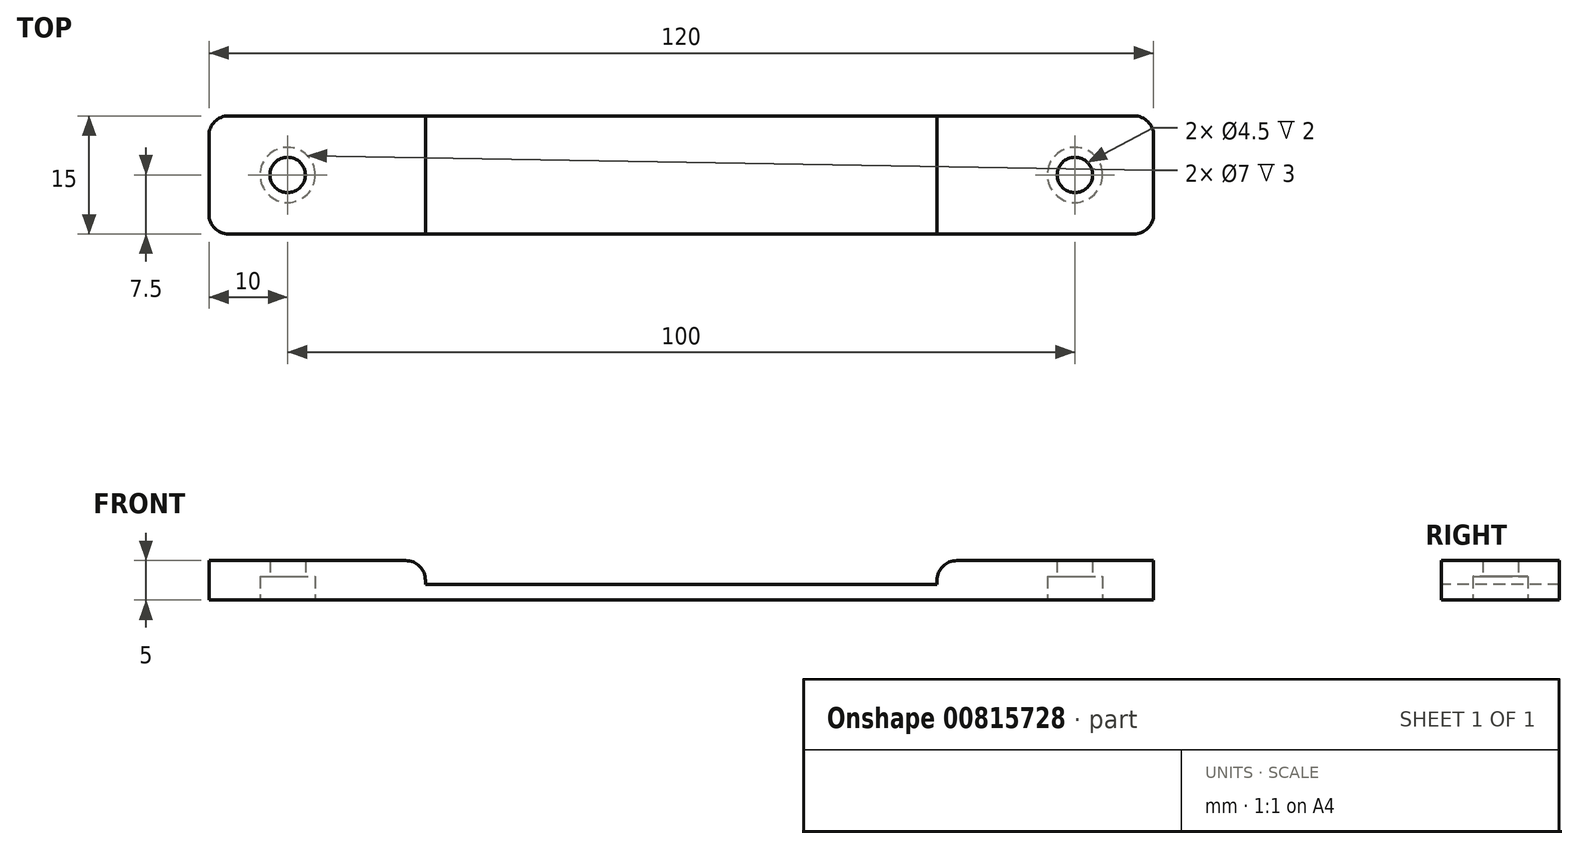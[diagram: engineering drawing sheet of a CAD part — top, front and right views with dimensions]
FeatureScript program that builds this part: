
annotation { "Feature Type Name" : "Feature", "Feature Type Description" : "" }
export const myFeature = defineFeature(function(context is Context, id is Id, definition is map)
    precondition{}
    {
        {
            var Q0;
            Q0=qCreatedBy(makeId("Top.planeOp"),FACE);
            var sketch = newSketch(context, id + "F0", { "sketchPlane" : qUnion([Q0])});
            skLineSegment(sketch, "E0.bottom", {"start": v(60, -7.5) * mm, "end": v(-60, -7.5) * mm});
            skLineSegment(sketch, "E0.top", {"start": v(60, 7.5) * mm, "end": v(-60, 7.5) * mm});
            skLineSegment(sketch, "E0.left", {"start": v(60, -7.5) * mm, "end": v(60, 7.5) * mm});
            skLineSegment(sketch, "E0.right", {"start": v(-60, -7.5) * mm, "end": v(-60, 7.5) * mm});
            skPoint(sketch, "E0.middle", {"position": v(0, 0) * mm});
            skSolve(sketch);
        }
        {
            var Q0;
            Q0=makeQuery(id+"F0.imprint","IMPRINT",FACE,{"disambiguationData":[TD([[makeQuery(id+"F0.imprint","IMPRINT",EDGE,{"derivedFrom":sQuery(id+"F0.wireOp",EDGE,"E0.bottom")}),-1.0]])]});
            extrude(context, id + "F1", {"entities" : qUnion([Q0]), "depth" : 2 * mm, "offsetDistance" : 25 * mm});
        }
        {
            var Q0;
            Q0=makeQuery(id+"F1.opExtrude","CAP_FACE",FACE,{"disambiguationData":[OSD([sQuery(id+"F0.wireOp",EDGE,"E0.bottom"),sQuery(id+"F0.wireOp",EDGE,"E0.top"),sQuery(id+"F0.wireOp",EDGE,"E0.left"),sQuery(id+"F0.wireOp",EDGE,"E0.right")])],"isStart":false});
            var sketch = newSketch(context, id + "F2", { "sketchPlane" : qUnion([Q0])});
            skLineSegment(sketch, "E1.bottom", {"start": v(-60, 7.5) * mm, "end": v(-32.5, 7.5) * mm});
            skLineSegment(sketch, "E1.top", {"start": v(-60, -7.5) * mm, "end": v(-32.5, -7.5) * mm});
            skLineSegment(sketch, "E1.left", {"start": v(-60, 7.5) * mm, "end": v(-60, -7.5) * mm});
            skLineSegment(sketch, "E1.right", {"start": v(-32.5, 7.5) * mm, "end": v(-32.5, -7.5) * mm});
            skLineSegment(sketch, "E2.bottom", {"start": v(60, 7.5) * mm, "end": v(32.5, 7.5) * mm});
            skLineSegment(sketch, "E2.top", {"start": v(60, -7.5) * mm, "end": v(32.5, -7.5) * mm});
            skLineSegment(sketch, "E2.left", {"start": v(60, 7.5) * mm, "end": v(60, -7.5) * mm});
            skLineSegment(sketch, "E2.right", {"start": v(32.5, 7.5) * mm, "end": v(32.5, -7.5) * mm});
            skSolve(sketch);
        }
        {
            var Q0;
            Q0=makeQuery(id+"F2.imprint","IMPRINT",FACE,{"disambiguationData":[TD([[makeQuery(id+"F2.imprint","IMPRINT",EDGE,{"derivedFrom":sQuery(id+"F2.wireOp",EDGE,"E1.bottom")}),1.0]])]});
            var Q1;
            Q1=makeQuery(id+"F2.imprint","IMPRINT",FACE,{"disambiguationData":[TD([[makeQuery(id+"F2.imprint","IMPRINT",EDGE,{"derivedFrom":sQuery(id+"F2.wireOp",EDGE,"E2.bottom")}),1.0]])]});
            extrude(context, id + "F3", {"entities" : qUnion([Q0, Q1]), "operationType" : NewBodyOperationType.ADD, "depth" : 3 * mm, "offsetDistance" : 25 * mm});
        }
        {
            var Q0;
            Q0=makeQuery(id+"F1.opExtrude","CAP_FACE",FACE,{"disambiguationData":[OSD([sQuery(id+"F0.wireOp",EDGE,"E0.bottom"),sQuery(id+"F0.wireOp",EDGE,"E0.top"),sQuery(id+"F0.wireOp",EDGE,"E0.left"),sQuery(id+"F0.wireOp",EDGE,"E0.right")])],"isStart":true});
            var sketch = newSketch(context, id + "F4", { "sketchPlane" : qUnion([Q0])});
            skCircle(sketch, "E3", {"center": v(-50, 0) * mm, "radius": 2.25 * mm});
            skCircle(sketch, "E4.1.0.0", {"center": v(50, 0) * mm, "radius": 2.25 * mm});
            skLineSegment(sketch, "E4.direction1", {"start": v(-50, 0) * mm, "end": v(50, 0) * mm, "construction": true});
            skCircle(sketch, "E5", {"center": v(-50, 0) * mm, "radius": 3.5 * mm});
            skCircle(sketch, "E6.1.0.0", {"center": v(50, 0) * mm, "radius": 3.5 * mm});
            skSolve(sketch);
        }
        {
            var Q0;
            Q0=makeQuery(id+"F4.imprint","IMPRINT",FACE,{"disambiguationData":[TD([[makeQuery(id+"F4.imprint","IMPRINT",EDGE,{"derivedFrom":sQuery(id+"F4.wireOp",EDGE,"E3")}),1.0]])]});
            var Q1;
            Q1=makeQuery(id+"F4.imprint","IMPRINT",FACE,{"disambiguationData":[TD([[makeQuery(id+"F4.imprint","IMPRINT",EDGE,{"derivedFrom":sQuery(id+"F4.wireOp",EDGE,"E4.1.0.0")}),1.0]])]});
            extrude(context, id + "F5", {"entities" : qUnion([Q0, Q1]), "operationType" : NewBodyOperationType.REMOVE, "oppositeDirection" : true, "depth" : 5 * mm, "offsetDistance" : 25 * mm});
        }
        {
            var Q0;
            Q0=makeQuery(id+"F3.boolean.opBoolean","MERGE",EDGE,{"derivedFrom":[makeQuery(id+"F1.opExtrude","SWEPT_EDGE",EDGE,{"disambiguationData":[OSD([sQuery(id+"F0.wireOp",EDGE,"E0.top"),sQuery(id+"F0.wireOp",EDGE,"E0.left")])]}),makeQuery(id+"F3.opExtrude","SWEPT_EDGE",EDGE,{"disambiguationData":[OSD([sQuery(id+"F2.wireOp",EDGE,"E2.bottom"),sQuery(id+"F2.wireOp",EDGE,"E2.left")])]})]});
            var Q1;
            Q1=makeQuery(id+"F3.boolean.opBoolean","MERGE",EDGE,{"derivedFrom":[makeQuery(id+"F1.opExtrude","SWEPT_EDGE",EDGE,{"disambiguationData":[OSD([sQuery(id+"F0.wireOp",EDGE,"E0.bottom"),sQuery(id+"F0.wireOp",EDGE,"E0.left")])]}),makeQuery(id+"F3.opExtrude","SWEPT_EDGE",EDGE,{"disambiguationData":[OSD([sQuery(id+"F2.wireOp",EDGE,"E2.top"),sQuery(id+"F2.wireOp",EDGE,"E2.left")])]})]});
            var Q2;
            Q2=makeQuery(id+"F3.boolean.opBoolean","MERGE",EDGE,{"derivedFrom":[makeQuery(id+"F1.opExtrude","SWEPT_EDGE",EDGE,{"disambiguationData":[OSD([sQuery(id+"F0.wireOp",EDGE,"E0.top"),sQuery(id+"F0.wireOp",EDGE,"E0.right")])]}),makeQuery(id+"F3.opExtrude","SWEPT_EDGE",EDGE,{"disambiguationData":[OSD([sQuery(id+"F2.wireOp",EDGE,"E1.bottom"),sQuery(id+"F2.wireOp",EDGE,"E1.left")])]})]});
            var Q3;
            Q3=makeQuery(id+"F3.boolean.opBoolean","MERGE",EDGE,{"derivedFrom":[makeQuery(id+"F1.opExtrude","SWEPT_EDGE",EDGE,{"disambiguationData":[OSD([sQuery(id+"F0.wireOp",EDGE,"E0.bottom"),sQuery(id+"F0.wireOp",EDGE,"E0.right")])]}),makeQuery(id+"F3.opExtrude","SWEPT_EDGE",EDGE,{"disambiguationData":[OSD([sQuery(id+"F2.wireOp",EDGE,"E1.top"),sQuery(id+"F2.wireOp",EDGE,"E1.left")])]})]});
            var Q4;
            Q4=makeQuery(id+"F3.opExtrude","CAP_EDGE",EDGE,{"disambiguationData":[OSD([sQuery(id+"F2.wireOp",EDGE,"E2.right")])],"isStart":false});
            var Q5;
            Q5=makeQuery(id+"F3.opExtrude","CAP_EDGE",EDGE,{"disambiguationData":[OSD([sQuery(id+"F2.wireOp",EDGE,"E1.right")])],"isStart":false});
            fillet(context, id + "F6", {"entities" : qUnion([Q0, Q1, Q2, Q3, Q4, Q5]), "tangentPropagation" : true, "radius" : 2.5 * mm, "defaultsChanged" : false, "vertexSettings" : [], "allowEdgeOverflow" : false});
        }
        {
            var Q0;
            Q0=makeQuery(id+"F4.imprint","IMPRINT",FACE,{"disambiguationData":[TD([[makeQuery(id+"F4.imprint","IMPRINT",EDGE,{"derivedFrom":sQuery(id+"F4.wireOp",EDGE,"E3")}),-1.0]])]});
            var Q1;
            Q1=makeQuery(id+"F4.imprint","IMPRINT",FACE,{"disambiguationData":[TD([[makeQuery(id+"F4.imprint","IMPRINT",EDGE,{"derivedFrom":sQuery(id+"F4.wireOp",EDGE,"E4.1.0.0")}),-1.0]])]});
            extrude(context, id + "F7", {"entities" : qUnion([Q0, Q1]), "operationType" : NewBodyOperationType.REMOVE, "oppositeDirection" : true, "depth" : 3 * mm, "offsetDistance" : 25 * mm});
        }
    });
